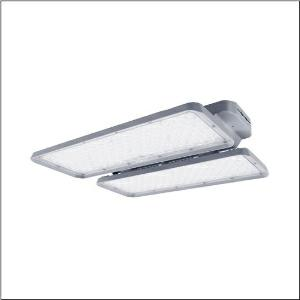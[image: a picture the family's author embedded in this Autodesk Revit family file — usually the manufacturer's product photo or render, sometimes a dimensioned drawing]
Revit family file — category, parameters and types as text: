
# Revit family: highbay_21-l_51hk42db4qca
name_source: partatom
category: Lighting Fixtures
units: mm (PartAtom-declared; Revit-internal decimal feet)

## family parameters
Cut with Voids When Loaded = No
Host = Face
Light Source = No
Part Type = Normal
Room Calculation Point = No
Round Connector Dimension = Use Diameter
Shared = No

## types (1)
- Highbay 21-L (1 x LED, 36000 lm, 200 W, 4000K)
    Apparent Load = 200 VA
    CIE Flux Codes = 75 96 99 100 100
    Color Rendering = 80
    Color Temperature = 4000K
    Default Elevation = 1800 mm
    Description = Highbay 21-L, LED high bay luminaire, primary light control with lens, of PC, light emission: direct distribution, primary light characteristic: symmetric, installation type: suspended mounting, surface-mounted, LED, rated luminous flux: 36.000lm, luminous efficacy: 180lm/W, light colour: 840, colour temperature: 4000K, with terminal, 5-pole, max. 2.5mm², mains connection: 220..240V, AC, 50Hz, rated input power: 200W, housing, of diecast aluminium, coated, grey, length: 471mm, width: 390mm, height: 87mm, protection rating (complete): IP66, insulation class (complete): insulation class I (protective earthing), certification: CE, ENEC, UKCA, protection symbol: D, impact resistance: IK08, permissible operating ambient temperature: -30..+60°C, corresponds to IFS (International Featured Standards) requirements for safety and quality in the food industry, LABS conformity tested according to VDMA 24364:2018-05, packaging unit: 1 piece
    Height = 89 mm
    Lamp = 1 x LED
    Lamp Light Flux = 36000 lm
    Lamp Power = 200 W
    Lamp count = 1
    Length = 471 mm
    Luminous efficacy = 180 lm/W
    Manufacturer = Siteco
    ModVariant = No
    Model = 51HK42DB4QCA
    Mounting Place = Ceiling
    Mounting Type = Pendant
    Number of Poles = 1
    OnlyDefault = Yes
    Power Factor = 1
    Product Name = Highbay 21-L
    Product group = LED high bay luminaire
    ProductGroupID = 903
    Protection Class = Protection class I
    Protection Degree = IP 66
    RLX_Detail_Level = 1
    RLX_Emergency_Light_Flux = 0 lm
    RLX_Emergency_Type = 0
    RLX_Emergency_Type_DB = No
    RlxData = <blob elided: 25957 chars, md5=7de11a29>
    Socket = socket
    Standby Power = 0 W
    System Light Flux = 36000 lm
    System Power = 200 W
    Type Comments = Product without accessories
    Type Image = l_1276530.jpg
    URL = http://relux.com
    VarID = ---
    Voltage = 0 V
    Weight = 0.00 kg
    Width = 390 mm

## geometry (parser evidence)
native form markers: Blend x4, Sweep x12
no freeform markers — native parametric forms only
